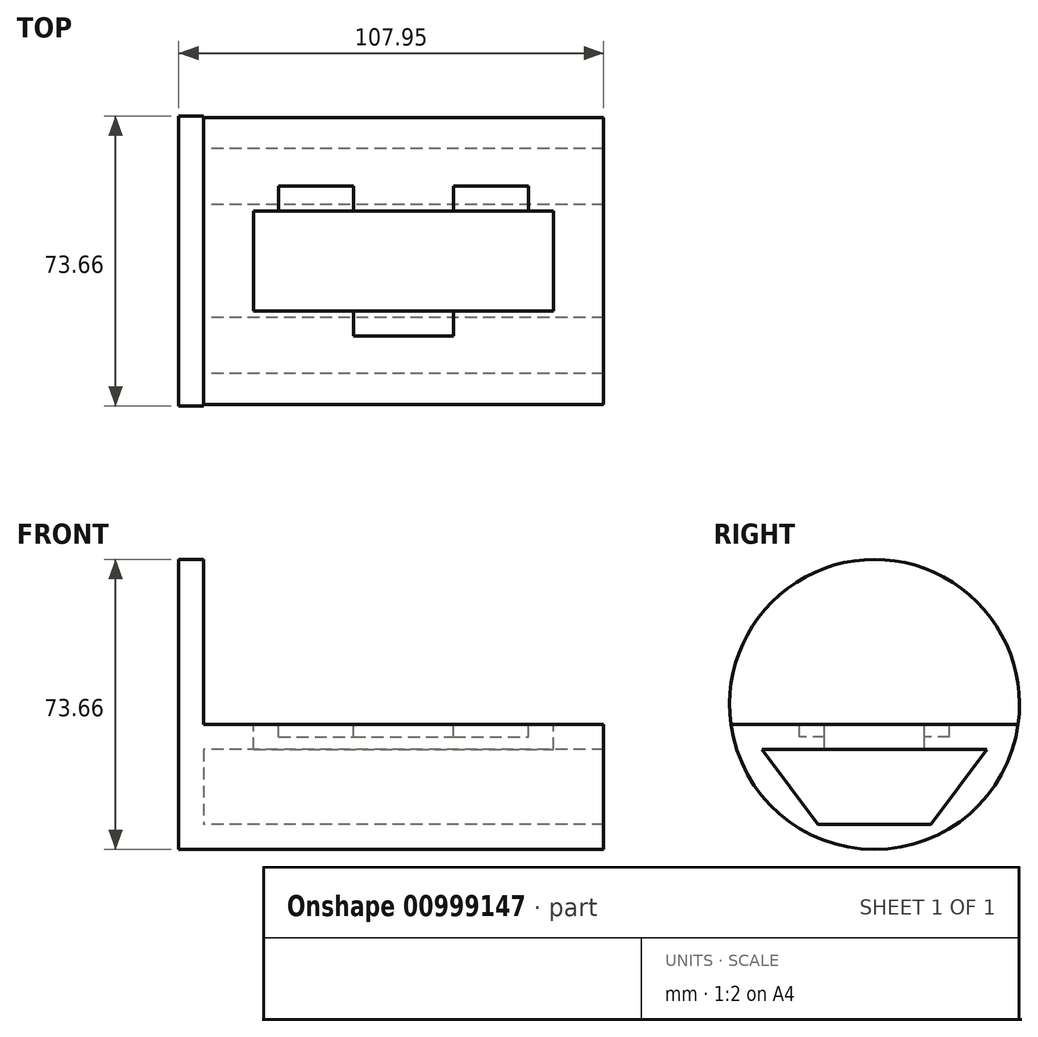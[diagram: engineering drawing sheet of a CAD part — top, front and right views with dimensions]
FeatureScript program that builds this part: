
annotation { "Feature Type Name" : "Feature", "Feature Type Description" : "" }
export const myFeature = defineFeature(function(context is Context, id is Id, definition is map)
    precondition{}
    {
        {
            var Q0;
            Q0=qCreatedBy(makeId("Right.planeOp"),FACE);
            var sketch = newSketch(context, id + "F0", { "sketchPlane" : qUnion([Q0])});
            skCircle(sketch, "E0", {"center": v(0, 0) * mm, "radius": 36.83 * mm});
            skSolve(sketch);
        }
        {
            var Q0;
            Q0=makeQuery(id+"F0.imprint","IMPRINT",FACE,{"disambiguationData":[TD([[makeQuery(id+"F0.imprint","IMPRINT",EDGE,{"derivedFrom":sQuery(id+"F0.wireOp",EDGE,"E0")}),1.0]])]});
            var sketch = newSketch(context, id + "F1", { "sketchPlane" : qUnion([Q0])});
            skLineSegment(sketch, "E1.bottom", {"start": v(-20.67, -30.48) * mm, "end": v(20.67, -30.48) * mm});
            skPoint(sketch, "E2", {"position": v(20.67, -30.48) * mm});
            skPoint(sketch, "E3", {"position": v(-20.67, -30.48) * mm});
            skLineSegment(sketch, "E4", {"start": v(12.75, -11.43) * mm, "end": v(35.01, -11.43) * mm});
            skLineSegment(sketch, "E5", {"start": v(-18.88, -11.43) * mm, "end": v(-35, -11.44) * mm});
            skLineSegment(sketch, "E6", {"start": v(12.75, -11.43) * mm, "end": v(-18.88, -11.43) * mm});
            skLineSegment(sketch, "E7", {"start": v(0, -36.83) * mm, "end": v(0, -30.48) * mm});
            skLineSegment(sketch, "E8", {"start": v(0, -30.48) * mm, "end": v(0, -11.43) * mm});
            skLineSegment(sketch, "E9", {"start": v(36.48, -5.08) * mm, "end": v(-36.48, -5.08) * mm});
            skLineSegment(sketch, "E10", {"start": v(0, 0) * mm, "end": v(0, -11.43) * mm});
            skLineSegment(sketch, "E11", {"start": v(-6.28, -5.08) * mm, "end": v(-6.28, -11.43) * mm});
            skLineSegment(sketch, "E12", {"start": v(-35, -11.44) * mm, "end": v(-28.57, -11.43) * mm});
            skLineSegment(sketch, "E13", {"start": v(-20.67, -30.48) * mm, "end": v(-14.32, -30.48) * mm});
            skLineSegment(sketch, "E14", {"start": v(20.67, -30.48) * mm, "end": v(14.32, -30.48) * mm});
            skLineSegment(sketch, "E15", {"start": v(35.01, -11.43) * mm, "end": v(28.58, -11.43) * mm});
            skLineSegment(sketch, "E16", {"start": v(28.58, -11.43) * mm, "end": v(14.32, -30.48) * mm});
            skLineSegment(sketch, "E17", {"start": v(-28.57, -11.43) * mm, "end": v(-14.32, -30.48) * mm});
            skLineSegment(sketch, "E18", {"start": v(-28.57, -11.43) * mm, "end": v(-28.58, -5.08) * mm});
            skLineSegment(sketch, "E19", {"start": v(28.58, -11.43) * mm, "end": v(28.58, -5.08) * mm});
            skLineSegment(sketch, "E20", {"start": v(-28.57, -8.26) * mm, "end": v(28.58, -8.26) * mm});
            skSolve(sketch);
        }
        {
            var Q0;
            {var subQ1=sQuery(id+"F1.wireOp",EDGE,"E5");var subQ5=sQuery(id+"F1.wireOp",EDGE,"E6");var subQ6=makeQuery(id+"F1.imprint","INTERSECT",VERTEX,{"derivedFrom":[subQ1,subQ5]});Q0=makeQuery(id+"F1.imprint","IMPRINT",FACE,{"disambiguationData":[TD([[makeQuery(id+"F1.imprint","IMPRINT",EDGE,{"disambiguationData":[TD([[subQ6,1.0]])],"derivedFrom":subQ5}),-1.0]])]});}
            var Q1;
            {var subQ0=sQuery(id+"F1.wireOp",EDGE,"E19");var subQ3=sQuery(id+"F1.wireOp",EDGE,"E20");var subQ4=makeQuery(id+"F1.imprint","INTERSECT",VERTEX,{"derivedFrom":[subQ0,subQ3]});Q1=makeQuery(id+"F1.imprint","IMPRINT",FACE,{"disambiguationData":[TD([[makeQuery(id+"F1.imprint","IMPRINT",EDGE,{"disambiguationData":[TD([[subQ4,1.0]])],"derivedFrom":subQ3}),-1.0]])]});}
            var Q2;
            {var subQ0=sQuery(id+"F1.wireOp",EDGE,"xOvHg0tn-TEt3-L2ib-0Wm1-0tn3J9Pu9Pb8");Q2=makeQuery(id+"F1.imprint","IMPRINT",FACE,{"disambiguationData":[TD([[makeQuery(id+"F1.imprint","IMPRINT",EDGE,{"derivedFrom":subQ0}),1.0]])]});}
            var Q3;
            {var subQ0=sQuery(id+"F1.wireOp",EDGE,"b1sQyHkT-liFX-Zt2v-cC6f-3GMuSH2HSxCr");Q3=makeQuery(id+"F1.imprint","IMPRINT",FACE,{"disambiguationData":[TD([[makeQuery(id+"F1.imprint","IMPRINT",EDGE,{"derivedFrom":subQ0}),-1.0]])]});}
            var Q4;
            {var subQ3=sQuery(id+"F1.wireOp",EDGE,"tBNurBHI-iiEl-UDbp-ZbHp-QAcbBZfyp1oP");Q4=makeQuery(id+"F1.imprint","IMPRINT",FACE,{"disambiguationData":[TD([[makeQuery(id+"F1.imprint","IMPRINT",EDGE,{"derivedFrom":subQ3}),1.0]])]});}
            var Q5;
            {var subQ3=sQuery(id+"F1.wireOp",EDGE,"T7q5g9tG-IPWu-WYv1-VDKW-RcaV8io13oG5");Q5=makeQuery(id+"F1.imprint","IMPRINT",FACE,{"disambiguationData":[TD([[makeQuery(id+"F1.imprint","IMPRINT",EDGE,{"derivedFrom":subQ3}),-1.0]])]});}
            var Q6;
            {var subQ0=sQuery(id+"F1.wireOp",EDGE,"E7");Q6=makeQuery(id+"F1.imprint","IMPRINT",FACE,{"disambiguationData":[TD([[makeQuery(id+"F1.imprint","IMPRINT",EDGE,{"derivedFrom":subQ0}),1.0]])]});}
            var Q7;
            {var subQ0=sQuery(id+"F1.wireOp",EDGE,"E7");Q7=makeQuery(id+"F1.imprint","IMPRINT",FACE,{"disambiguationData":[TD([[makeQuery(id+"F1.imprint","IMPRINT",EDGE,{"derivedFrom":subQ0}),-1.0]])]});}
            var Q8;
            {var subQ0=sQuery(id+"F1.wireOp",EDGE,"E11");var subQ1=sQuery(id+"F1.wireOp",EDGE,"E9");var subQ2=makeQuery(id+"F1.imprint","INTERSECT",VERTEX,{"derivedFrom":[subQ1,subQ0]});var subQ9=sQuery(id+"F1.wireOp",EDGE,"E6");var subQ10=makeQuery(id+"F1.imprint","INTERSECT",VERTEX,{"derivedFrom":[subQ9,subQ0]});Q8=qUnion([makeQuery(id+"F1.imprint","IMPRINT",FACE,{"disambiguationData":[TD([[makeQuery(id+"F1.imprint","IMPRINT",EDGE,{"disambiguationData":[TD([[subQ10,1.0]])],"derivedFrom":subQ0}),1.0]])]}),makeQuery(id+"F1.imprint","IMPRINT",FACE,{"disambiguationData":[TD([[makeQuery(id+"F1.imprint","IMPRINT",EDGE,{"disambiguationData":[TD([[subQ2,1.0]])],"derivedFrom":subQ1}),1.0]])]})]);}
            var Q9;
            {var subQ0=sQuery(id+"F1.wireOp",EDGE,"E18");var subQ4=sQuery(id+"F1.wireOp",EDGE,"E9");var subQ5=makeQuery(id+"F1.imprint","INTERSECT",VERTEX,{"derivedFrom":[subQ4,subQ0]});Q9=makeQuery(id+"F1.imprint","IMPRINT",FACE,{"disambiguationData":[TD([[makeQuery(id+"F1.imprint","IMPRINT",EDGE,{"disambiguationData":[TD([[subQ5,-1.0]])],"derivedFrom":subQ4}),1.0]])]});}
            var Q10;
            {var subQ0=sQuery(id+"F1.wireOp",EDGE,"E11");var subQ1=sQuery(id+"F1.wireOp",EDGE,"E9");var subQ2=makeQuery(id+"F1.imprint","INTERSECT",VERTEX,{"derivedFrom":[subQ1,subQ0]});Q10=makeQuery(id+"F1.imprint","IMPRINT",FACE,{"disambiguationData":[TD([[makeQuery(id+"F1.imprint","IMPRINT",EDGE,{"disambiguationData":[TD([[subQ2,-1.0]])],"derivedFrom":subQ1}),1.0]])]});}
            var Q11;
            {var subQ0=sQuery(id+"F1.wireOp",EDGE,"E19");var subQ1=sQuery(id+"F1.wireOp",EDGE,"E9");var subQ2=makeQuery(id+"F1.imprint","INTERSECT",VERTEX,{"derivedFrom":[subQ1,subQ0]});Q11=makeQuery(id+"F1.imprint","IMPRINT",FACE,{"disambiguationData":[TD([[makeQuery(id+"F1.imprint","IMPRINT",EDGE,{"disambiguationData":[TD([[subQ2,-1.0]])],"derivedFrom":subQ1}),1.0]])]});}
            var Q12;
            {var subQ0=sQuery(id+"F1.wireOp",EDGE,"E19");var subQ6=sQuery(id+"F1.wireOp",EDGE,"E9");var subQ7=makeQuery(id+"F1.imprint","INTERSECT",VERTEX,{"derivedFrom":[subQ6,subQ0]});Q12=makeQuery(id+"F1.imprint","IMPRINT",FACE,{"disambiguationData":[TD([[makeQuery(id+"F1.imprint","IMPRINT",EDGE,{"disambiguationData":[TD([[subQ7,1.0]])],"derivedFrom":subQ6}),1.0]])]});}
            var Q13;
            {var subQ0=sQuery(id+"F1.wireOp",EDGE,"E16");Q13=makeQuery(id+"F1.imprint","IMPRINT",FACE,{"disambiguationData":[TD([[makeQuery(id+"F1.imprint","IMPRINT",EDGE,{"derivedFrom":subQ0}),1.0]])]});}
            var Q14;
            {var subQ0=sQuery(id+"F1.wireOp",EDGE,"E17");Q14=makeQuery(id+"F1.imprint","IMPRINT",FACE,{"disambiguationData":[TD([[makeQuery(id+"F1.imprint","IMPRINT",EDGE,{"derivedFrom":subQ0}),-1.0]])]});}
            extrude(context, id + "F2", {"entities" : qUnion([Q0, Q1, Q2, Q3, Q4, Q5, Q6, Q7, Q8, Q9, Q10, Q11, Q12, Q13, Q14]), "depth" : 101.6 * mm, "offsetDistance" : 25.4 * mm});
        }
        {
            var Q0;
            Q0 = qSketchRegion(id + "F0", true);
            extrude(context, id + "F3", {"entities" : qUnion([Q0]), "operationType" : NewBodyOperationType.ADD, "oppositeDirection" : true, "depth" : 6.35 * mm, "offsetDistance" : 25.4 * mm});
        }
        {
            var Q0;
            Q0=makeQuery(id+"F2.opExtrude","SWEPT_FACE",FACE,{"disambiguationData":[OSD([sQuery(id+"F1.wireOp",EDGE,"E9")])]});
            var sketch = newSketch(context, id + "F4", { "sketchPlane" : qUnion([Q0])});
            skPoint(sketch, "E21.startSnap0", {"position": v(101.6, 0) * mm});
            skLineSegment(sketch, "E22.bottom", {"start": v(12.7, 12.7) * mm, "end": v(50.8, 12.7) * mm});
            skLineSegment(sketch, "E22.top", {"start": v(12.7, -12.7) * mm, "end": v(50.8, -12.7) * mm});
            skLineSegment(sketch, "E22.left", {"start": v(12.7, 12.7) * mm, "end": v(12.7, -12.7) * mm});
            skPoint(sketch, "E22.middle", {"position": v(31.75, 0) * mm});
            skLineSegment(sketch, "E23.bottom", {"start": v(12.7, -12.7) * mm, "end": v(88.9, -12.7) * mm});
            skLineSegment(sketch, "E23.top", {"start": v(12.7, -19.05) * mm, "end": v(88.9, -19.05) * mm});
            skLineSegment(sketch, "E23.left", {"start": v(12.7, -12.7) * mm, "end": v(12.7, -19.05) * mm});
            skLineSegment(sketch, "E23.right", {"start": v(88.9, -12.7) * mm, "end": v(88.9, -19.05) * mm});
            skLineSegment(sketch, "E24.bottom", {"start": v(12.7, 12.7) * mm, "end": v(88.9, 12.7) * mm});
            skLineSegment(sketch, "E24.top", {"start": v(12.7, 19.05) * mm, "end": v(88.9, 19.05) * mm});
            skLineSegment(sketch, "E24.left", {"start": v(12.7, 12.7) * mm, "end": v(12.7, 19.05) * mm});
            skLineSegment(sketch, "E24.right", {"start": v(88.9, 12.7) * mm, "end": v(88.9, 19.05) * mm});
            skLineSegment(sketch, "E25", {"start": v(12.7, -15.88) * mm, "end": v(38.1, -15.88) * mm});
            skLineSegment(sketch, "E26", {"start": v(38.1, -12.7) * mm, "end": v(38.1, -19.05) * mm});
            skLineSegment(sketch, "E27", {"start": v(88.9, -15.88) * mm, "end": v(63.5, -15.88) * mm});
            skLineSegment(sketch, "E28", {"start": v(63.5, -12.7) * mm, "end": v(63.5, -19.05) * mm});
            skLineSegment(sketch, "E29", {"start": v(12.7, 15.87) * mm, "end": v(19.05, 15.88) * mm});
            skLineSegment(sketch, "E30", {"start": v(19.05, 15.88) * mm, "end": v(19.05, 19.05) * mm});
            skLineSegment(sketch, "E31", {"start": v(19.05, 19.05) * mm, "end": v(19.05, 12.7) * mm});
            skLineSegment(sketch, "E32", {"start": v(88.9, 15.88) * mm, "end": v(82.55, 15.88) * mm});
            skLineSegment(sketch, "E33", {"start": v(82.55, 15.88) * mm, "end": v(82.55, 19.05) * mm});
            skLineSegment(sketch, "E34", {"start": v(82.55, 19.05) * mm, "end": v(82.55, 12.7) * mm});
            skLineSegment(sketch, "E35", {"start": v(50.8, 12.7) * mm, "end": v(50.8, 19.05) * mm});
            skLineSegment(sketch, "E36", {"start": v(50.8, 15.88) * mm, "end": v(38.1, 15.88) * mm});
            skLineSegment(sketch, "E37", {"start": v(50.8, 15.88) * mm, "end": v(63.5, 15.88) * mm});
            skLineSegment(sketch, "E38", {"start": v(38.1, 19.05) * mm, "end": v(38.1, 12.7) * mm});
            skLineSegment(sketch, "E39", {"start": v(0, 0) * mm, "end": v(12.7, 0) * mm});
            skLineSegment(sketch, "E40", {"start": v(88.9, 12.7) * mm, "end": v(88.9, -12.7) * mm});
            skLineSegment(sketch, "E41", {"start": v(101.6, 0) * mm, "end": v(88.9, 0) * mm});
            skLineSegment(sketch, "E42", {"start": v(63.5, 19.05) * mm, "end": v(63.5, 12.7) * mm});
            skSolve(sketch);
        }
        {
            var Q0;
            {var subQ12=sQuery(id+"F4.wireOp",EDGE,"E22.bottom");var subQ15=makeQuery(id+"F4.imprint","INTERSECT",VERTEX,{"derivedFrom":[subQ12,sQuery(id+"F4.wireOp",EDGE,"E31")]});Q0=makeQuery(id+"F4.imprint","IMPRINT",FACE,{"disambiguationData":[TD([[makeQuery(id+"F4.imprint","IMPRINT",EDGE,{"disambiguationData":[TD([[subQ15,-1.0]])],"derivedFrom":subQ12}),-1.0]])]});}
            extrude(context, id + "F5", {"entities" : qUnion([Q0]), "operationType" : NewBodyOperationType.REMOVE, "oppositeDirection" : true, "depth" : 6.35 * mm, "offsetDistance" : 25.4 * mm});
        }
        {
            var Q0;
            {var subQ2=sQuery(id+"F4.wireOp",EDGE,"E22.top");var subQ4=sQuery(id+"F4.wireOp",EDGE,"E23.bottom");var subQ5=makeQuery(id+"F4.imprint","INTERSECT",VERTEX,{"derivedFrom":[subQ2,subQ4]});Q0=makeQuery(id+"F4.imprint","IMPRINT",FACE,{"disambiguationData":[TD([[makeQuery(id+"F4.imprint","IMPRINT",EDGE,{"disambiguationData":[TD([[subQ5,1.0]])],"derivedFrom":subQ2}),-1.0]])]});}
            var Q1;
            {var subQ1=sQuery(id+"F4.wireOp",EDGE,"E30");Q1=makeQuery(id+"F4.imprint","IMPRINT",FACE,{"disambiguationData":[TD([[makeQuery(id+"F4.imprint","IMPRINT",EDGE,{"derivedFrom":subQ1}),-1.0]])]});}
            var Q2;
            {var subQ0=sQuery(id+"F4.wireOp",EDGE,"E33");Q2=makeQuery(id+"F4.imprint","IMPRINT",FACE,{"disambiguationData":[TD([[makeQuery(id+"F4.imprint","IMPRINT",EDGE,{"derivedFrom":subQ0}),1.0]])]});}
            extrude(context, id + "F6", {"entities" : qUnion([Q0, Q1, Q2]), "operationType" : NewBodyOperationType.REMOVE, "oppositeDirection" : true, "depth" : 3.17 * mm, "offsetDistance" : 25.4 * mm});
        }
    });
